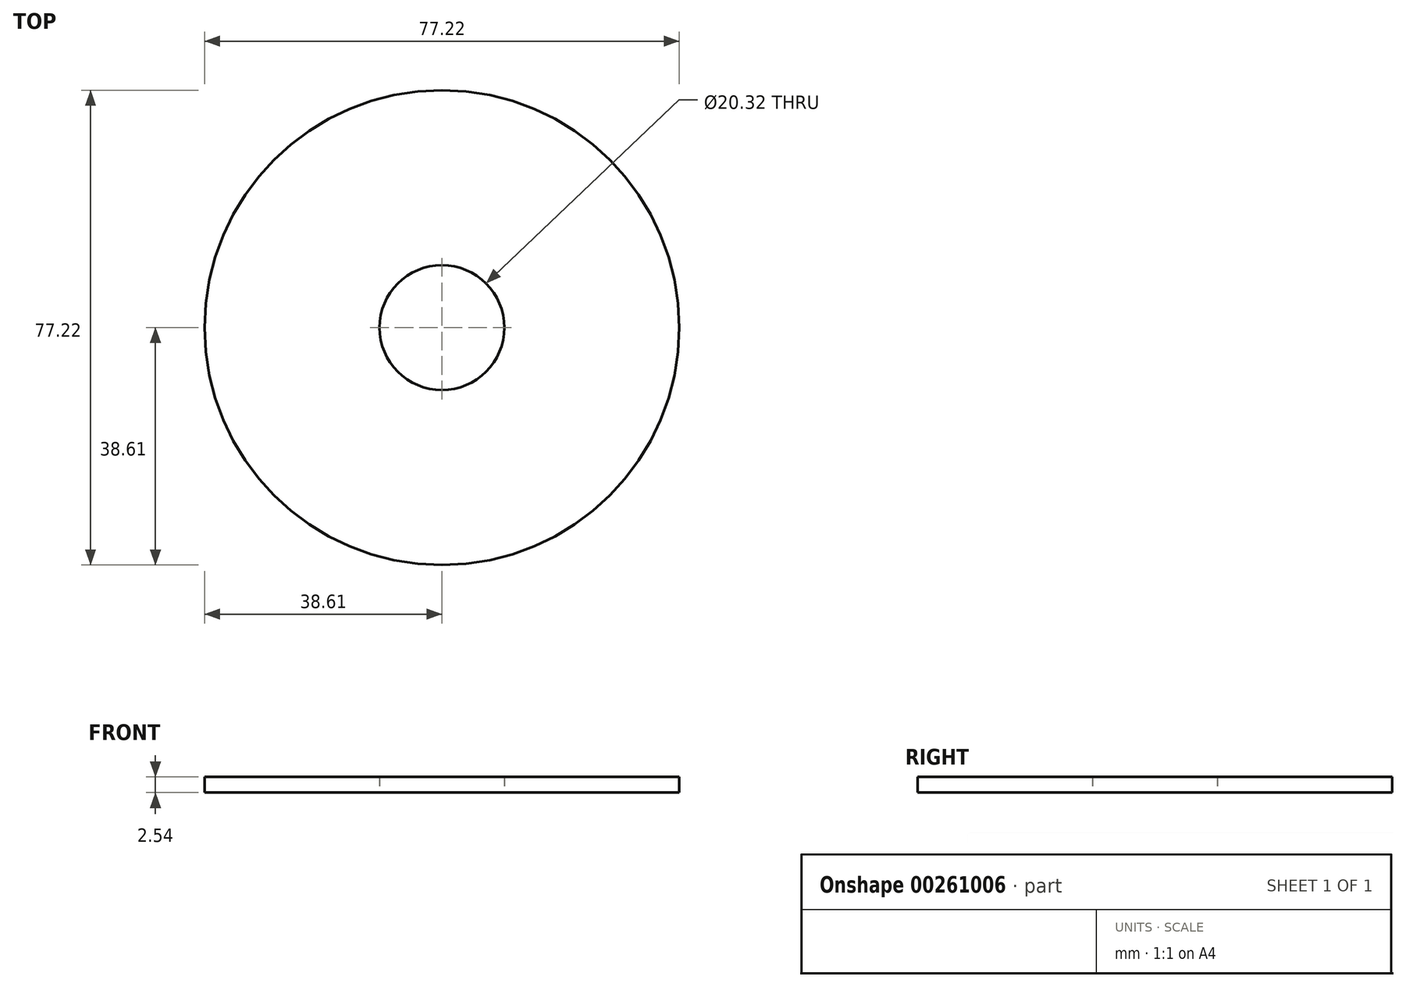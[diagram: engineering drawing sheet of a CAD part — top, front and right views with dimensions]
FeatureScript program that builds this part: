
annotation { "Feature Type Name" : "Feature", "Feature Type Description" : "" }
export const myFeature = defineFeature(function(context is Context, id is Id, definition is map)
    precondition{}
    {
        {
            var Q0;
            Q0=qCreatedBy(makeId("Front.planeOp"),FACE);
            var sketch = newSketch(context, id + "F0", { "sketchPlane" : qUnion([Q0])});
            skLineSegment(sketch, "E0.bottom", {"start": v(10.16, 1.22) * mm, "end": v(38.6, 1.22) * mm});
            skLineSegment(sketch, "E0.top", {"start": v(10.16, -1.32) * mm, "end": v(38.6, -1.32) * mm});
            skLineSegment(sketch, "E0.left", {"start": v(10.16, 1.22) * mm, "end": v(10.16, -1.32) * mm});
            skLineSegment(sketch, "E0.right", {"start": v(38.6, 1.22) * mm, "end": v(38.6, -1.32) * mm});
            skLineSegment(sketch, "E1", {"start": v(0, 30.53) * mm, "end": v(0, -15.9) * mm, "construction": true});
            skSolve(sketch);
        }
        {
            var Q0;
            Q0=sQuery(id+"F0.wireOp",EDGE,"E0.right");
            var Q1;
            Q1=sQuery(id+"F0.wireOp",EDGE,"E0.left");
            var Q2;
            Q2=sQuery(id+"F0.wireOp",EDGE,"E0.top");
            var Q3;
            Q3=sQuery(id+"F0.wireOp",EDGE,"E0.bottom");
            var Q4;
            Q4=sQuery(id+"F0.wireOp",EDGE,"E1");
            revolve(context, id + "F1", {"bodyType" : ToolBodyType.SURFACE, "surfaceEntities" : qUnion([Q0, Q1, Q2, Q3]), "axis" : qUnion([Q4]), "revolveType" : RevolveType.FULL});
        }
    });
